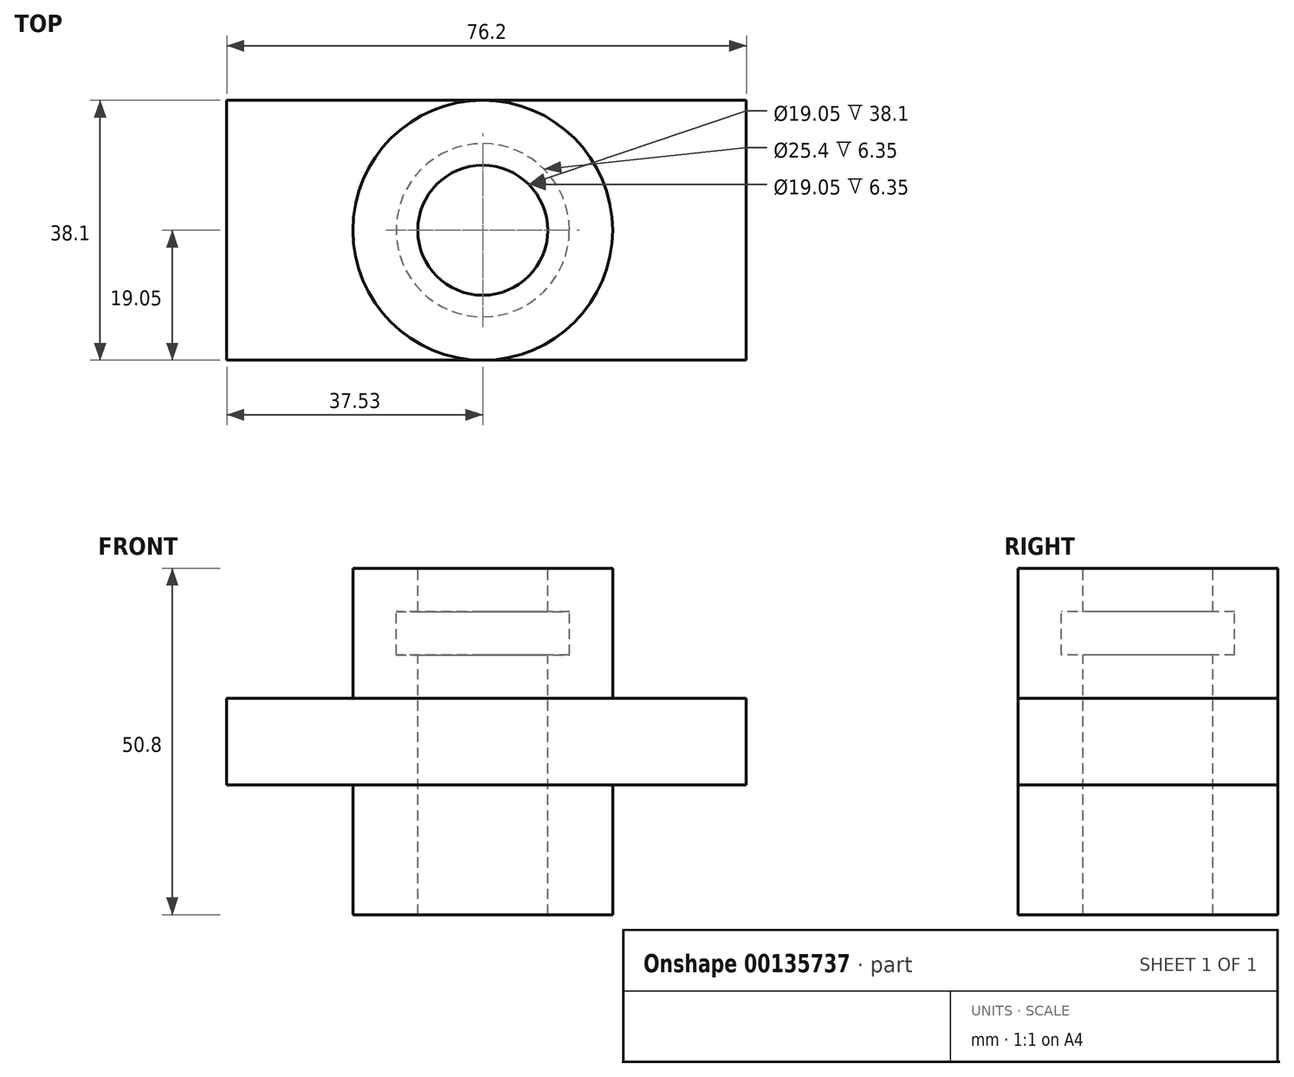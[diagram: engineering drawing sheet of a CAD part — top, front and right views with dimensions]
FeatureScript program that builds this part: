
annotation { "Feature Type Name" : "Feature", "Feature Type Description" : "" }
export const myFeature = defineFeature(function(context is Context, id is Id, definition is map)
    precondition{}
    {
        {
            var Q0;
            Q0=qCreatedBy(makeId("Front.planeOp"),FACE);
            var sketch = newSketch(context, id + "F0", { "sketchPlane" : qUnion([Q0])});
            skLineSegment(sketch, "E0", {"start": v(0, 91.23) * mm, "end": v(0, -71.56) * mm, "construction": true});
            skLineSegment(sketch, "E1", {"start": v(-9.53, 0) * mm, "end": v(-19.05, 0) * mm});
            skLineSegment(sketch, "E2", {"start": v(-19.05, 0) * mm, "end": v(-19.05, 50.8) * mm});
            skLineSegment(sketch, "E3", {"start": v(-19.05, 50.8) * mm, "end": v(-9.52, 50.8) * mm});
            skLineSegment(sketch, "E4", {"start": v(-9.53, 50.8) * mm, "end": v(-9.53, 44.45) * mm});
            skLineSegment(sketch, "E5", {"start": v(-9.52, 44.45) * mm, "end": v(-12.7, 44.45) * mm});
            skLineSegment(sketch, "E6", {"start": v(-12.7, 44.45) * mm, "end": v(-12.7, 38.1) * mm});
            skLineSegment(sketch, "E7", {"start": v(-12.7, 38.1) * mm, "end": v(-9.52, 38.1) * mm});
            skLineSegment(sketch, "E8", {"start": v(-9.53, 38.1) * mm, "end": v(-9.53, 0) * mm});
            skSolve(sketch);
        }
        {
            var Q0;
            Q0 = qSketchRegion(id + "F0", true);
            var Q1;
            Q1=sQuery(id+"F0.wireOp",EDGE,"E0");
            revolve(context, id + "F1", {"entities" : qUnion([Q0]), "axis" : qUnion([Q1]), "revolveType" : RevolveType.FULL});
        }
        {
            var Q0;
            Q0=qCreatedBy(makeId("Right.planeOp"),FACE);
            var sketch = newSketch(context, id + "F2", { "sketchPlane" : qUnion([Q0])});
            skLineSegment(sketch, "E9.bottom", {"start": v(-38.67, 31.75) * mm, "end": v(37.53, 31.75) * mm});
            skLineSegment(sketch, "E9.top", {"start": v(-38.67, 19.05) * mm, "end": v(37.53, 19.05) * mm});
            skLineSegment(sketch, "E9.left", {"start": v(-38.67, 31.75) * mm, "end": v(-38.67, 19.05) * mm});
            skLineSegment(sketch, "E9.right", {"start": v(37.53, 31.75) * mm, "end": v(37.53, 19.05) * mm});
            skSolve(sketch);
        }
        {
            var Q0;
            Q0 = qSketchRegion(id + "F2", true);
            extrude(context, id + "F3", {"entities" : qUnion([Q0]), "operationType" : NewBodyOperationType.ADD, "endBound" : BoundingType.SYMMETRIC, "depth" : 38.1 * mm});
        }
        {
            var Q0;
            Q0=makeQuery(id+"F3.boolean.opBoolean","SPLIT",FACE,{"disambiguationData":[TD([makeQuery(id+"F1.opRevolve","SWEPT_FACE",FACE,{"disambiguationData":[OSD([sQuery(id+"F0.wireOp",EDGE,"E8")])]})])],"derivedFrom":makeQuery(id+"F3.opExtrude","SWEPT_FACE",FACE,{"disambiguationData":[OSD([sQuery(id+"F2.wireOp",EDGE,"E9.bottom")])]})});
            extrude(context, id + "F4", {"entities" : qUnion([Q0]), "operationType" : NewBodyOperationType.REMOVE, "oppositeDirection" : true, "depth" : 25.4 * mm});
        }
        {
            var Q0;
            Q0=makeQuery(id+"F1.opRevolve","SWEPT_BODY",BODY,{"disambiguationData":[OSD([sQuery(id+"F0.wireOp",EDGE,"E1"),sQuery(id+"F0.wireOp",EDGE,"E2"),sQuery(id+"F0.wireOp",EDGE,"E3"),sQuery(id+"F0.wireOp",EDGE,"E4"),sQuery(id+"F0.wireOp",EDGE,"E5"),sQuery(id+"F0.wireOp",EDGE,"E6"),sQuery(id+"F0.wireOp",EDGE,"E7"),sQuery(id+"F0.wireOp",EDGE,"E8")])]});
            var Q1;
            Q1=makeQuery(id+"F1.opRevolve","SWEPT_EDGE",EDGE,{"disambiguationData":[OSD([sQuery(id+"F0.wireOp",EDGE,"E3"),sQuery(id+"F0.wireOp",EDGE,"E4")])]});
            transform(context, id + "F5", {"entities" : qUnion([Q0]), "transformType" : TransformType.ROTATION, "transformAxis" : qUnion([Q1]), "angle" : 90 * degree, "makeCopy" : false});
        }
    });
